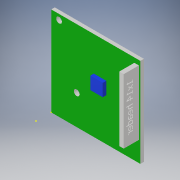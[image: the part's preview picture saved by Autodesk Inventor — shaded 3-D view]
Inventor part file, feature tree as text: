
AUTODESK INVENTOR PART (.ipt)
format: ipt  version: 2017 (Build 210142000, 142)  size: 384,000 bytes
history: native  units: in
note: dims shown in document units (in); Inventor stores cm internally (conversion verified against a paired STEP export)
features: sketch x6, extrude x4
ambient origin geometry x8: Origin, YZ Plane, XZ Plane, XY Plane, X Axis, Y Axis, Z Axis, Center Point
bodies: Solid3 (feature_tree), Solid4 (feature_tree)
feature tree (10):
  sketch  "Sketch1"  dims[d0=1.9685in d1=1.9685in]
  sketch  "Sketch2"  dims[d2=0.126in d3=0.126in]
  sketch  "Sketch7"  dims[d23=0.126in d28=0.2756in]
  extrude  "Extrusion4"  Depth=1.9685in
  extrude  "Extrusion5"  Depth=0.126in
  extrude  "Extrusion6"  Depth=0.2756in
  sketch  "Sketch9"  dims[d31=90.0deg]
  extrude  "Extrusion7"  Depth=0.2756in
  sketch  "Sketch8"  dims[d29=0.2756in d30=0.2756in]
  sketch  "Sketch14"  dims[d32=0.2756in d33=0.2756in d34=0.2756in d35=90.0deg d36=0.0787in d37=0.0in d38=0.0787in d39=0.0in d47=0.3346in d48=0.0in d49=0.3937in d50=0.0in]
